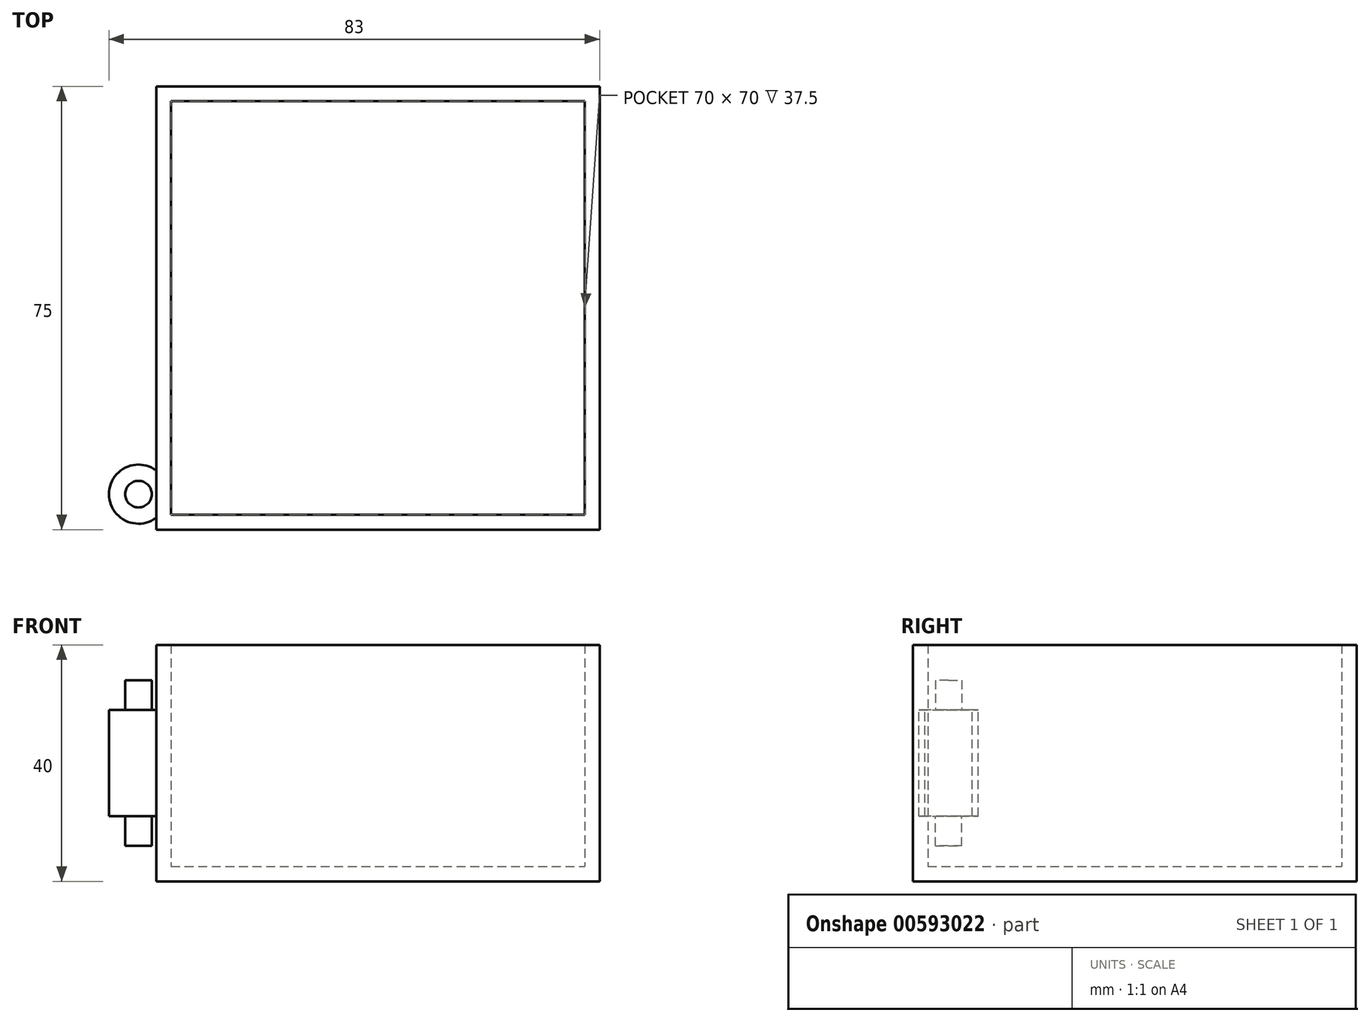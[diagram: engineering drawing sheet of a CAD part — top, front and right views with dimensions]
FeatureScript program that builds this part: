
annotation { "Feature Type Name" : "Feature", "Feature Type Description" : "" }
export const myFeature = defineFeature(function(context is Context, id is Id, definition is map)
    precondition{}
    {
        {
            var Q0;
            Q0=qCreatedBy(makeId("Top.planeOp"),FACE);
            var sketch = newSketch(context, id + "F0", { "sketchPlane" : qUnion([Q0])});
            skLineSegment(sketch, "E0.bottom", {"start": v(0, 0) * mm, "end": v(75, 0) * mm});
            skLineSegment(sketch, "E0.top", {"start": v(0, 75) * mm, "end": v(75, 75) * mm});
            skLineSegment(sketch, "E0.left", {"start": v(0, 0) * mm, "end": v(0, 75) * mm});
            skLineSegment(sketch, "E0.right", {"start": v(75, 0) * mm, "end": v(75, 75) * mm});
            skSolve(sketch);
        }
        {
            var Q0;
            Q0 = qSketchRegion(id + "F0", true);
            extrude(context, id + "F1", {"entities" : qUnion([Q0]), "depth" : 40 * mm, "offsetDistance" : 25 * mm});
        }
        {
            var Q0;
            Q0=makeQuery(id+"F1.opExtrude","CAP_FACE",FACE,{"disambiguationData":[OSD([sQuery(id+"F0.wireOp",EDGE,"E0.bottom"),sQuery(id+"F0.wireOp",EDGE,"E0.top"),sQuery(id+"F0.wireOp",EDGE,"E0.left"),sQuery(id+"F0.wireOp",EDGE,"E0.right")])],"isStart":false});
            shell(context, id + "F2", {"entities" : qUnion([Q0]), "thickness" : 2.5 * mm});
        }
        {
            var Q0;
            Q0=makeQuery(id+"F1.opExtrude","CAP_FACE",FACE,{"disambiguationData":[OSD([sQuery(id+"F0.wireOp",EDGE,"E0.bottom"),sQuery(id+"F0.wireOp",EDGE,"E0.top"),sQuery(id+"F0.wireOp",EDGE,"E0.left"),sQuery(id+"F0.wireOp",EDGE,"E0.right")])],"isStart":true});
            cPlane(context, id + "F3", {"entities" : qUnion([Q0]), "cplaneType" : CPlaneType.OFFSET, "offset" : 20 * mm, "oppositeDirection" : true, "width" : 150 * mm, "height" : 150 * mm});
        }
        {
            var Q0;
            Q0=qCreatedBy(id+"F3.planeOp",FACE);
            var sketch = newSketch(context, id + "F4", { "sketchPlane" : qUnion([Q0])});
            skArc(sketch, "E1", {"start": v(0, -2) * mm, "mid": v(-8, -6) * mm, "end": v(0, -10) * mm});
            skLineSegment(sketch, "E2", {"start": v(0, -10) * mm, "end": v(0, -2) * mm});
            skSolve(sketch);
        }
        {
            var Q0;
            Q0 = qSketchRegion(id + "F4", true);
            extrude(context, id + "F5", {"entities" : qUnion([Q0]), "operationType" : NewBodyOperationType.ADD, "endBound" : BoundingType.SYMMETRIC, "depth" : 18 * mm, "offsetDistance" : 25 * mm});
        }
        {
            var Q0;
            Q0=makeQuery(id+"F5.opExtrude","CAP_FACE",FACE,{"disambiguationData":[OSD([sQuery(id+"F4.wireOp",EDGE,"E1"),sQuery(id+"F4.wireOp",EDGE,"E2")])],"isStart":true});
            var sketch = newSketch(context, id + "F6", { "sketchPlane" : qUnion([Q0])});
            skCircle(sketch, "E3", {"center": v(-3, 6) * mm, "radius": 2.25 * mm});
            skSolve(sketch);
        }
        {
            var Q0;
            Q0=makeQuery(id+"F5.opExtrude","CAP_FACE",FACE,{"disambiguationData":[OSD([sQuery(id+"F4.wireOp",EDGE,"E1"),sQuery(id+"F4.wireOp",EDGE,"E2")])],"isStart":false});
            var sketch = newSketch(context, id + "F7", { "sketchPlane" : qUnion([Q0])});
            skCircle(sketch, "E4", {"center": v(-3, -6) * mm, "radius": 2.25 * mm});
            skSolve(sketch);
        }
        {
            var Q0;
            Q0 = qSketchRegion(id + "F7", true);
            extrude(context, id + "F8", {"entities" : qUnion([Q0]), "operationType" : NewBodyOperationType.ADD, "depth" : 5 * mm, "offsetDistance" : 25 * mm});
        }
        {
            var Q0;
            Q0=makeQuery(id+"F6.imprint","IMPRINT",FACE,{"disambiguationData":[TD([[makeQuery(id+"F6.imprint","IMPRINT",EDGE,{"derivedFrom":sQuery(id+"F6.wireOp",EDGE,"E3")}),1.0]])]});
            var Q1;
            Q1=sQuery(id+"F6.wireOp",EDGE,"E3");
            extrude(context, id + "F9", {"entities" : qUnion([Q0]), "operationType" : NewBodyOperationType.ADD, "surfaceEntities" : qUnion([Q1]), "depth" : 5 * mm, "offsetDistance" : 25 * mm});
        }
    });
